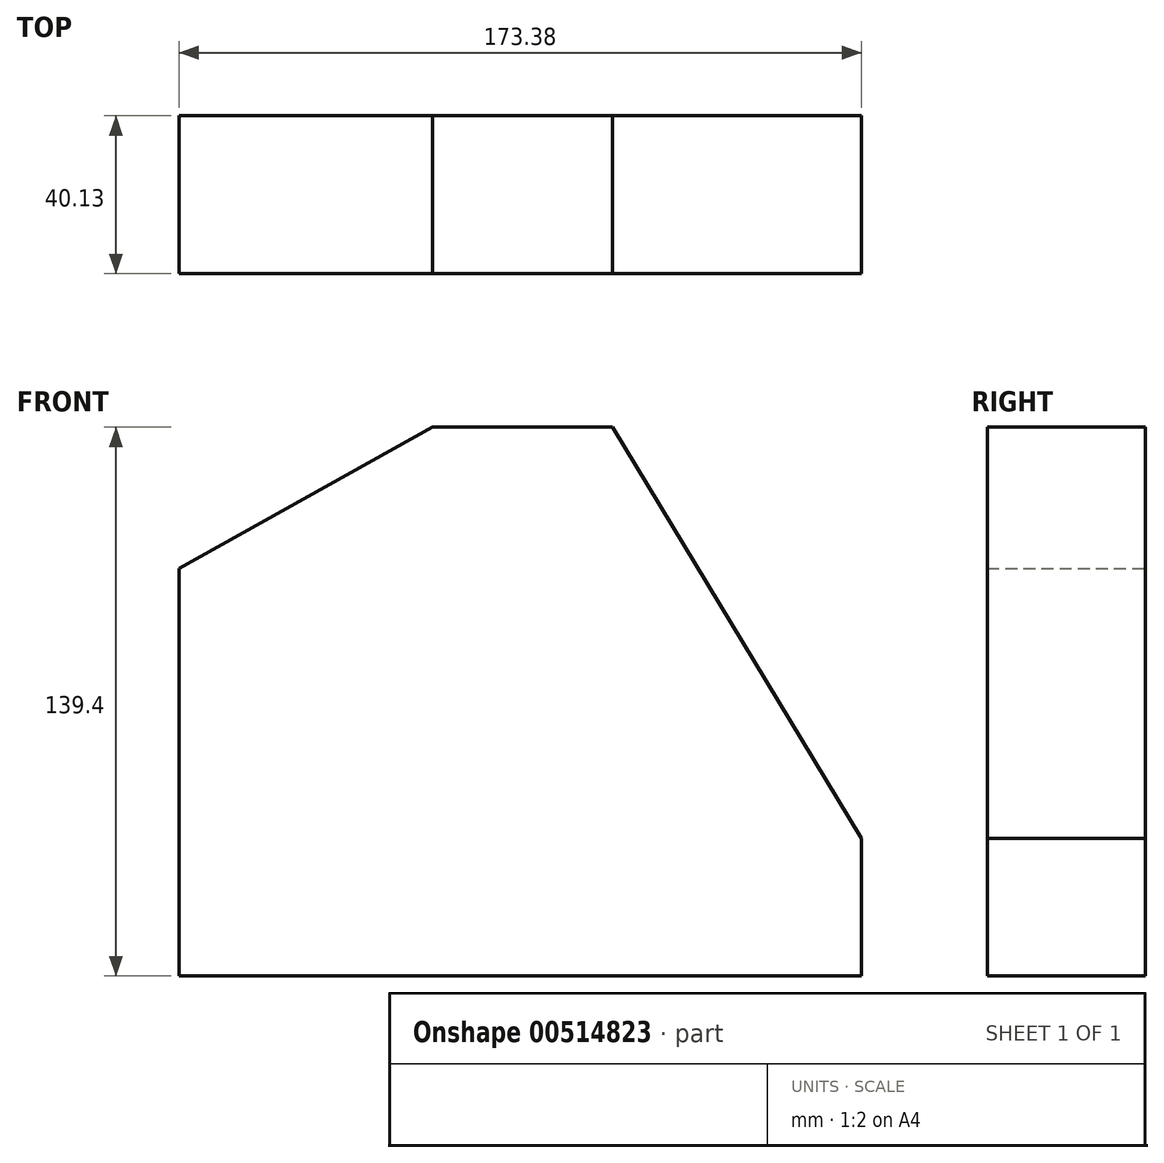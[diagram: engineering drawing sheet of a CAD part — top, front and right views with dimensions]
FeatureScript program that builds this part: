
annotation { "Feature Type Name" : "Feature", "Feature Type Description" : "" }
export const myFeature = defineFeature(function(context is Context, id is Id, definition is map)
    precondition{}
    {
        {
            var Q0;
            Q0=qCreatedBy(makeId("Front.planeOp"),FACE);
            var sketch = newSketch(context, id + "F0", { "sketchPlane" : qUnion([Q0])});
            skLineSegment(sketch, "E0.top", {"start": v(-78.75, -81.93) * mm, "end": v(94.63, -81.93) * mm});
            skLineSegment(sketch, "E1", {"start": v(-78.75, 21.6) * mm, "end": v(-14.29, 57.47) * mm});
            skLineSegment(sketch, "E2", {"start": v(31.44, 57.47) * mm, "end": v(94.63, -47) * mm});
            skLineSegment(sketch, "E3", {"start": v(-14.29, 57.47) * mm, "end": v(31.44, 57.47) * mm});
            skLineSegment(sketch, "E4", {"start": v(-78.75, 21.6) * mm, "end": v(-78.75, -81.93) * mm});
            skLineSegment(sketch, "E5", {"start": v(94.63, -47) * mm, "end": v(94.63, -81.93) * mm});
            skSolve(sketch);
        }
        {
            var Q0;
            Q0 = qSketchRegion(id + "F0", true);
            extrude(context, id + "F1", {"entities" : qUnion([Q0]), "depth" : 40.13 * mm, "offsetDistance" : 25.4 * mm});
        }
    });
